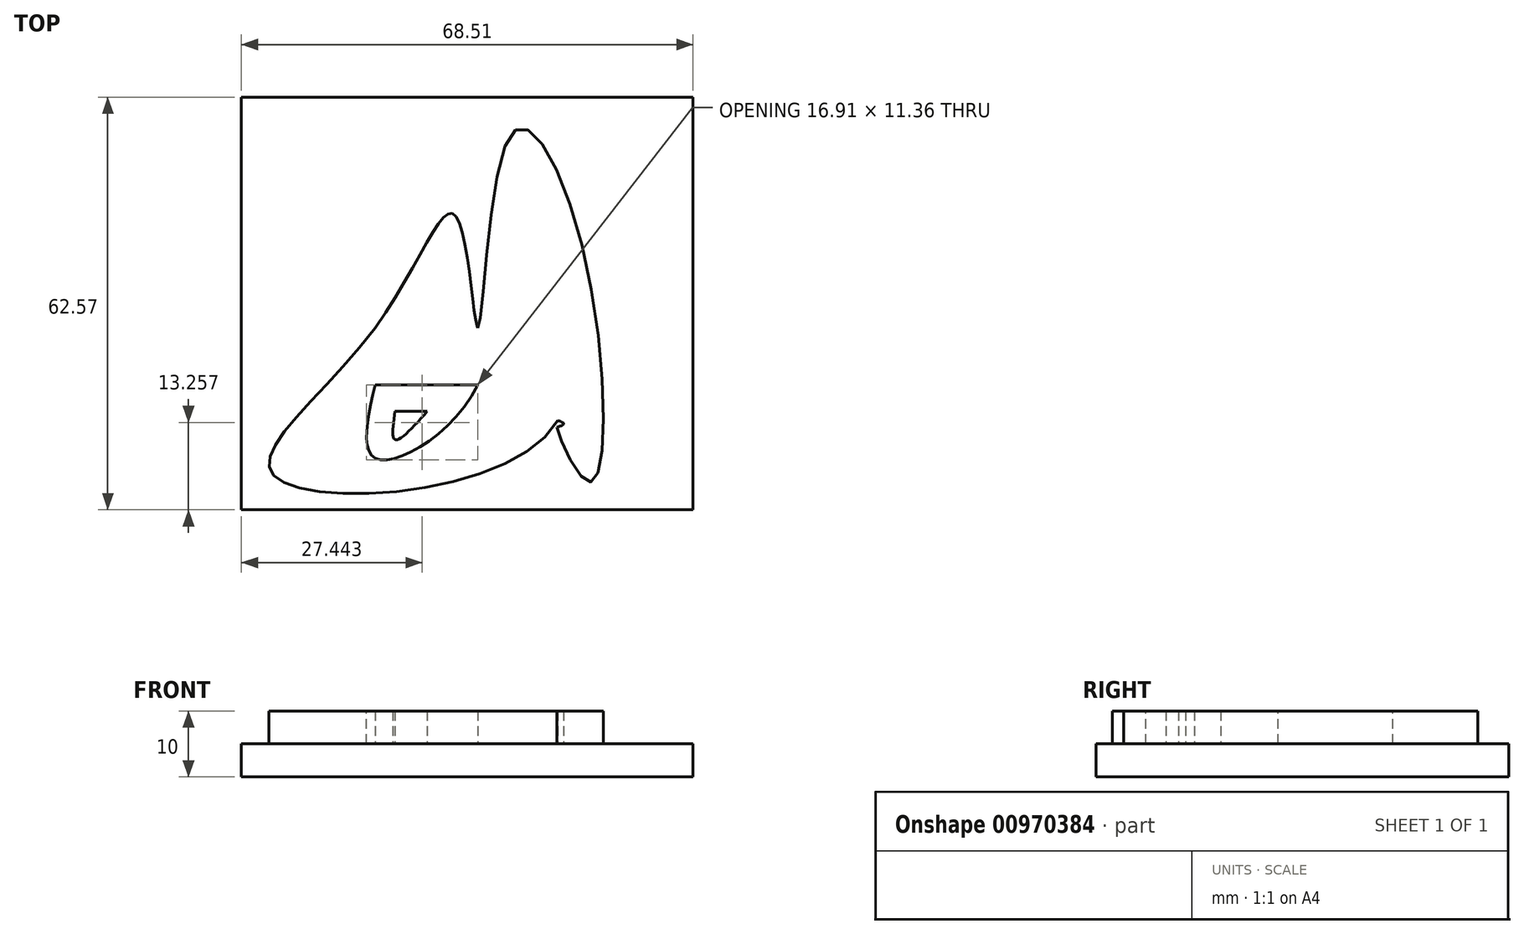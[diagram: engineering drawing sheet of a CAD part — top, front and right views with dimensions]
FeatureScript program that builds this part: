
annotation { "Feature Type Name" : "Feature", "Feature Type Description" : "" }
export const myFeature = defineFeature(function(context is Context, id is Id, definition is map)
    precondition{}
    {
        {
            var Q0;
            Q0=qCreatedBy(makeId("Top.planeOp"),FACE);
            var sketch = newSketch(context, id + "F0", { "sketchPlane" : qUnion([Q0])});
            skLineSegment(sketch, "E0.bottom", {"start": v(0, 0) * mm, "end": v(-15.61, 0) * mm});
            skLineSegment(sketch, "E0.top", {"start": v(0, -8.67) * mm, "end": v(-15.61, -8.67) * mm});
            skLineSegment(sketch, "E0.left", {"start": v(0, 0) * mm, "end": v(0, -8.67) * mm});
            skLineSegment(sketch, "E0.right", {"start": v(-15.61, 0) * mm, "end": v(-15.61, -8.67) * mm});
            skFitSpline(sketch, "E1", {"points": [v(-15.61, -8.67) * mm, v(-15.61, -19.75) * mm, v(0, -8.67) * mm, v(5.74, 8.4) * mm, v(12.1, -14.07) * mm, v(-30.83, -22.56) * mm, v(-15.61, 0) * mm, v(-3.32, 16.85) * mm, v(0, 0) * mm, v(5.01, 29.31) * mm, v(15.76, 12.58) * mm, v(16.78, -23.38) * mm, v(12, -15.09) * mm, v(12.13, -14.45) * mm], "startDerivative": vector(-57.9, -254.98) * mm, "endDerivative": vector(21.45, 23.1) * mm});
            skFitSpline(sketch, "E2", {"points": [v(12.1, -14.07) * mm, v(13.01, -14.55) * mm, v(12, -15.09) * mm], "startDerivative": vector(2.83, -1) * mm, "endDerivative": vector(-2.97, -1.06) * mm});
            skSolve(sketch);
        }
        {
            var Q0;
            {var subQ0=sQuery(id+"F0.wireOp",EDGE,"E0.bottom");Q0=makeQuery(id+"F0.imprint","IMPRINT",FACE,{"disambiguationData":[TD([[makeQuery(id+"F0.imprint","IMPRINT",EDGE,{"derivedFrom":subQ0}),-1.0]])]});}
            var Q1;
            {var subQ0=sQuery(id+"F0.wireOp",EDGE,"E0.right");Q1=makeQuery(id+"F0.imprint","IMPRINT",FACE,{"disambiguationData":[TD([[makeQuery(id+"F0.imprint","IMPRINT",EDGE,{"derivedFrom":subQ0}),-1.0]])]});}
            var Q2;
            {var subQ0=sQuery(id+"F0.wireOp",EDGE,"E0.left");Q2=makeQuery(id+"F0.imprint","IMPRINT",FACE,{"disambiguationData":[TD([[makeQuery(id+"F0.imprint","IMPRINT",EDGE,{"derivedFrom":subQ0}),1.0]])]});}
            var Q3;
            Q3=makeQuery(id+"F0.imprint","IMPRINT",FACE,{"disambiguationData":[TD([[makeQuery(id+"F0.imprint","IMPRINT",EDGE,{"derivedFrom":sQuery(id+"F0.wireOp",EDGE,"E0.bottom")}),1.0]])]});
            extrude(context, id + "F1", {"entities" : qUnion([Q0, Q1, Q2, Q3]), "depth" : 5 * mm, "offsetDistance" : 25 * mm});
        }
        {
            var Q0;
            Q0=qCreatedBy(makeId("Top.planeOp"),FACE);
            var sketch = newSketch(context, id + "F2", { "sketchPlane" : qUnion([Q0])});
            skLineSegment(sketch, "E3", {"start": v(-7.68, -12.68) * mm, "end": v(-12.58, -12.68) * mm});
            skFitSpline(sketch, "E4", {"points": [v(-12.58, -12.68) * mm, v(-12.58, -16.98) * mm, v(-7.68, -12.68) * mm], "startDerivative": vector(-1.99, -13.48) * mm, "endDerivative": vector(11.33, 12.58) * mm});
            skSolve(sketch);
        }
        {
            var Q0;
            Q0=makeQuery(id+"F2.imprint","IMPRINT",FACE,{"disambiguationData":[TD([[makeQuery(id+"F2.imprint","IMPRINT",EDGE,{"derivedFrom":sQuery(id+"F2.wireOp",EDGE,"E3")}),1.0]])]});
            extrude(context, id + "F3", {"entities" : qUnion([Q0]), "depth" : 5 * mm, "offsetDistance" : 25 * mm});
        }
        {
            var Q0;
            Q0=qCreatedBy(makeId("Top.planeOp"),FACE);
            var sketch = newSketch(context, id + "F4", { "sketchPlane" : qUnion([Q0])});
            skLineSegment(sketch, "E5.bottom", {"start": v(-35.9, -27.6) * mm, "end": v(32.61, -27.6) * mm});
            skLineSegment(sketch, "E5.top", {"start": v(-35.9, 34.96) * mm, "end": v(32.61, 34.96) * mm});
            skLineSegment(sketch, "E5.left", {"start": v(-35.9, -27.6) * mm, "end": v(-35.9, 34.96) * mm});
            skLineSegment(sketch, "E5.right", {"start": v(32.61, -27.6) * mm, "end": v(32.61, 34.96) * mm});
            skSolve(sketch);
        }
        {
            var Q0;
            Q0=makeQuery(id+"F4.imprint","IMPRINT",FACE,{"disambiguationData":[TD([[makeQuery(id+"F4.imprint","IMPRINT",EDGE,{"derivedFrom":sQuery(id+"F4.wireOp",EDGE,"E5.bottom")}),1.0]])]});
            extrude(context, id + "F5", {"entities" : qUnion([Q0]), "oppositeDirection" : true, "depth" : 5 * mm, "offsetDistance" : 25 * mm});
        }
    });
